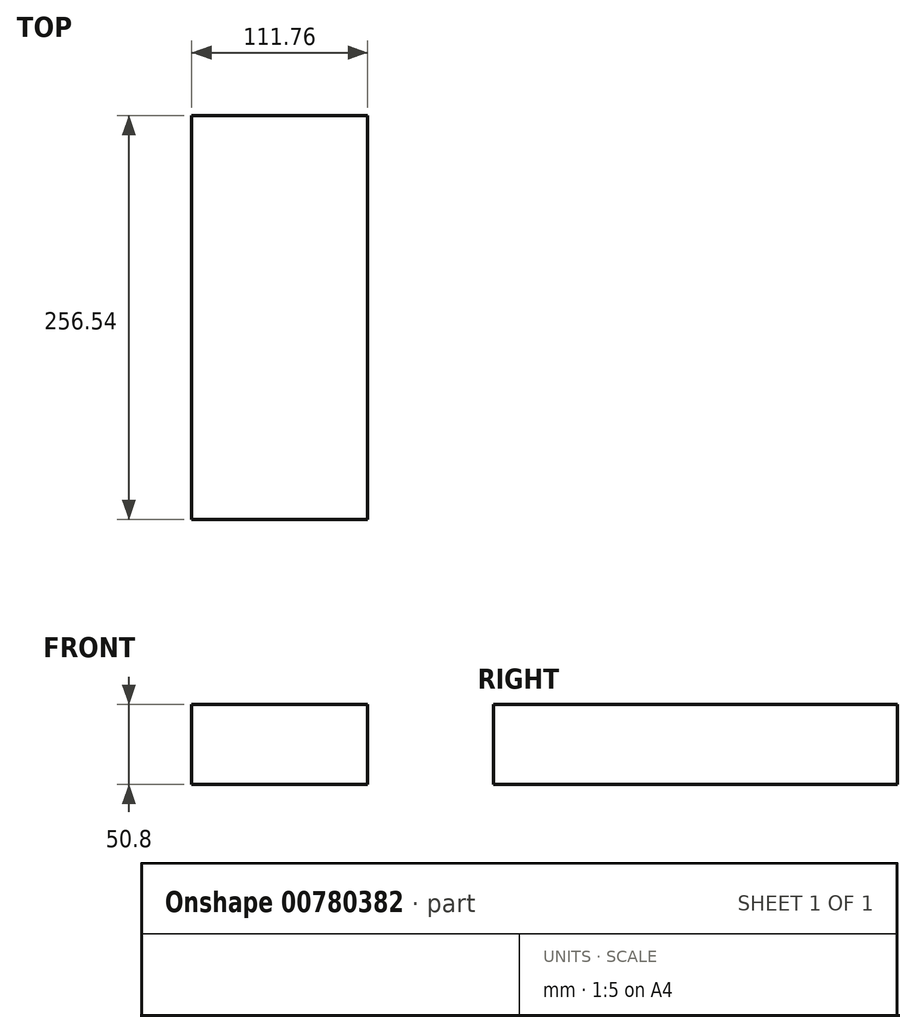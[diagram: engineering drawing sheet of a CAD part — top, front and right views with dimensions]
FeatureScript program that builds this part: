
annotation { "Feature Type Name" : "Feature", "Feature Type Description" : "" }
export const myFeature = defineFeature(function(context is Context, id is Id, definition is map)
    precondition{}
    {
        {
            var Q0;
            Q0=qCreatedBy(makeId("Top.planeOp"),FACE);
            var sketch = newSketch(context, id + "F0", { "sketchPlane" : qUnion([Q0])});
            skLineSegment(sketch, "E0.bottom", {"start": v(55.88, 128.27) * mm, "end": v(-55.88, 128.27) * mm});
            skLineSegment(sketch, "E0.top", {"start": v(55.88, -128.27) * mm, "end": v(-55.88, -128.27) * mm});
            skLineSegment(sketch, "E0.left", {"start": v(55.88, 128.27) * mm, "end": v(55.88, -128.27) * mm});
            skLineSegment(sketch, "E0.right", {"start": v(-55.88, 128.27) * mm, "end": v(-55.88, -128.27) * mm});
            skPoint(sketch, "E0.middle", {"position": v(0, 0) * mm});
            skSolve(sketch);
        }
        {
            var Q0;
            Q0=makeQuery(id+"F0.imprint","IMPRINT",FACE,{"disambiguationData":[TD([[makeQuery(id+"F0.imprint","IMPRINT",EDGE,{"derivedFrom":sQuery(id+"F0.wireOp",EDGE,"E0.bottom")}),1.0]])]});
            extrude(context, id + "F1", {"entities" : qUnion([Q0]), "depth" : 50.8 * mm, "offsetDistance" : 25 * mm});
        }
    });
